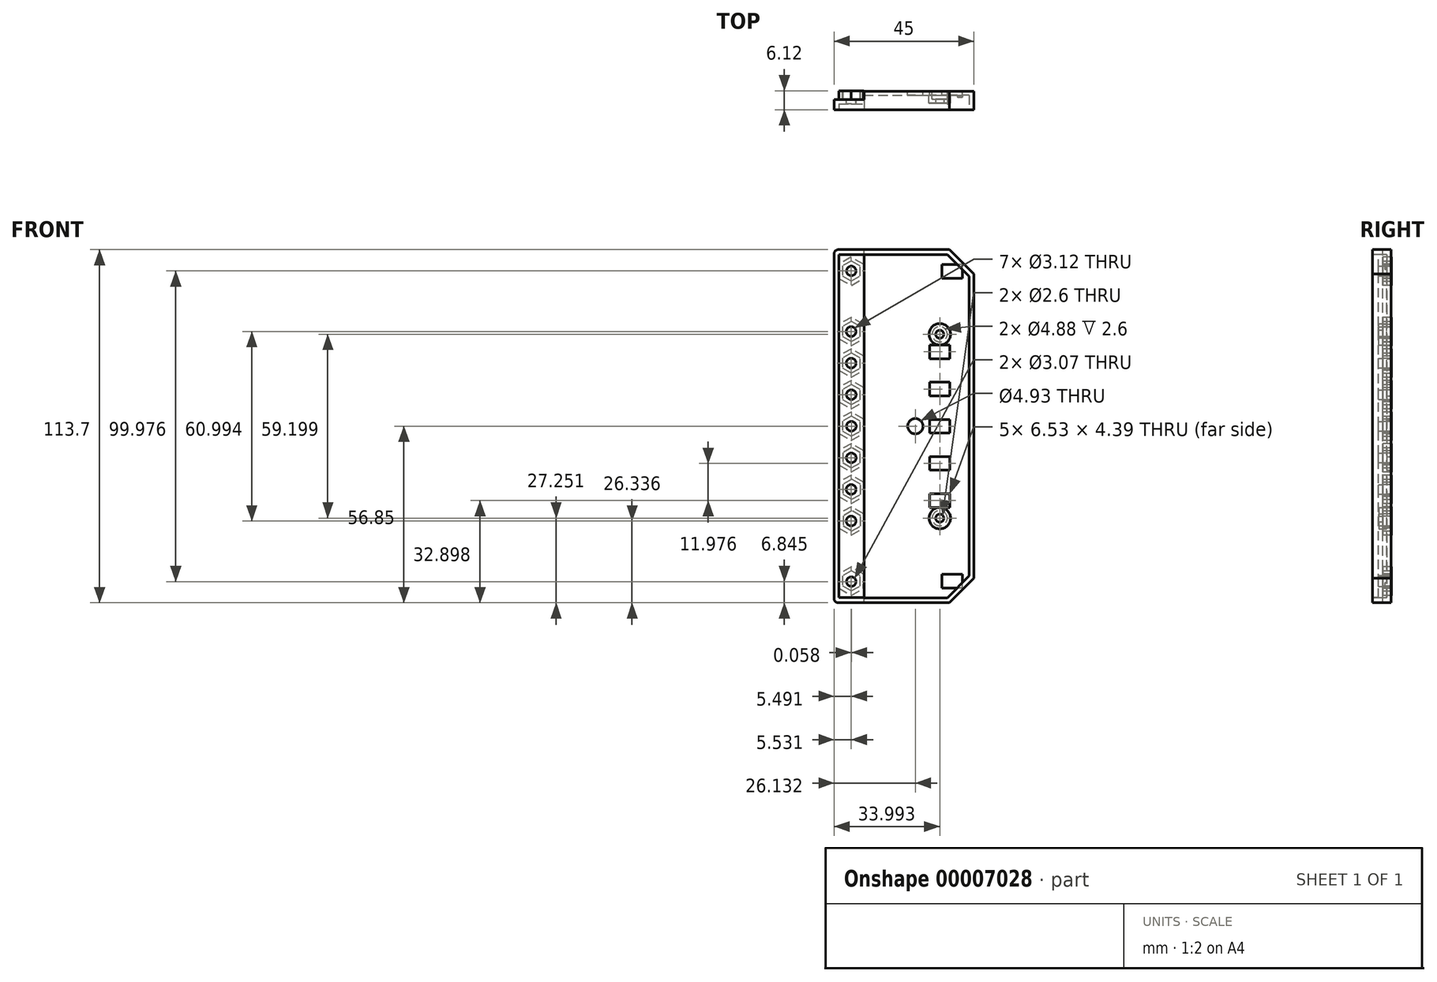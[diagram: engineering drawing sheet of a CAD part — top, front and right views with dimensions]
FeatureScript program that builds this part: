
annotation { "Feature Type Name" : "Feature", "Feature Type Description" : "" }
export const myFeature = defineFeature(function(context is Context, id is Id, definition is map)
    precondition{}
    {
        {
            var Q0;
            Q0=qCreatedBy(makeId("Top.planeOp"),FACE);
            var sketch = newSketch(context, id + "F0", { "sketchPlane" : qUnion([Q0])});
            skLineSegment(sketch, "E0.rect.bottom", {"start": v(22.5, -3) * mm, "end": v(-22.5, -3) * mm});
            skLineSegment(sketch, "E0.rect.top", {"start": v(22.5, 3) * mm, "end": v(-22.5, 3) * mm});
            skLineSegment(sketch, "E0.rect.left", {"start": v(22.5, -3) * mm, "end": v(22.5, 3) * mm});
            skLineSegment(sketch, "E0.rect.right", {"start": v(-22.5, -3) * mm, "end": v(-22.5, 3) * mm});
            skPoint(sketch, "E0.rect.middle", {"position": v(0, 0) * mm});
            skLineSegment(sketch, "E1", {"start": v(-12.85, 3) * mm, "end": v(-12.85, 0.3) * mm});
            skLineSegment(sketch, "E2", {"start": v(-12.85, 0.3) * mm, "end": v(-22.5, 0.3) * mm});
            skSolve(sketch);
        }
        {
            var Q0;
            Q0 = qSketchRegion(id + "F0", true);
            extrude(context, id + "F1", {"entities" : qUnion([Q0]), "oppositeDirection" : true, "depth" : 113.7 * mm});
        }
        {
            var Q0;
            {var subQ1=sQuery(id+"F0.wireOp",EDGE,"E1");Q0=makeQuery(id+"F0.imprint","IMPRINT",FACE,{"disambiguationData":[TD([[makeQuery(id+"F0.imprint","IMPRINT",EDGE,{"derivedFrom":subQ1}),-1.0]])]});}
            extrude(context, id + "F2", {"entities" : qUnion([Q0]), "operationType" : NewBodyOperationType.REMOVE, "oppositeDirection" : true, "depth" : 113.93 * mm});
        }
        {
            var Q0;
            Q0=makeQuery(id+"F1.opExtrude","SWEPT_FACE",FACE,{"disambiguationData":[OSD([sQuery(id+"F0.wireOp",EDGE,"E0.rect.bottom")])]});
            var sketch = newSketch(context, id + "F3", { "sketchPlane" : qUnion([Q0])});
            skLineSegment(sketch, "E3.bottom", {"start": v(-22.5, -113.59) * mm, "end": v(-12.85, -113.59) * mm});
            skLineSegment(sketch, "E3.top", {"start": v(-22.5, 0) * mm, "end": v(-12.85, 0) * mm});
            skLineSegment(sketch, "E3.left", {"start": v(-22.5, -113.59) * mm, "end": v(-22.5, 0) * mm});
            skLineSegment(sketch, "E3.right", {"start": v(-12.85, -113.59) * mm, "end": v(-12.85, 0) * mm});
            skLineSegment(sketch, "E4.bottom", {"start": v(-20.92, -112) * mm, "end": v(-12.85, -112) * mm});
            skLineSegment(sketch, "E4.top", {"start": v(-20.92, -1.58) * mm, "end": v(-12.85, -1.58) * mm});
            skLineSegment(sketch, "E4.left", {"start": v(-20.92, -112) * mm, "end": v(-20.92, -1.58) * mm});
            skLineSegment(sketch, "E4.right", {"start": v(-12.85, -112) * mm, "end": v(-12.85, -1.58) * mm});
            skSolve(sketch);
        }
        {
            var Q0;
            Q0=makeQuery(id+"F3.imprint","IMPRINT",FACE,{"disambiguationData":[TD([[makeQuery(id+"F3.imprint","IMPRINT",EDGE,{"derivedFrom":sQuery(id+"F3.wireOp",EDGE,"E4.bottom")}),1.0]])]});
            extrude(context, id + "F4", {"entities" : qUnion([Q0]), "operationType" : NewBodyOperationType.REMOVE, "oppositeDirection" : true, "depth" : 1.9 * mm});
        }
        {
            var Q0;
            Q0=makeQuery(id+"F1.opExtrude","CAP_EDGE",EDGE,{"disambiguationData":[OSD([sQuery(id+"F0.wireOp",EDGE,"E0.rect.left")])],"isStart":false});
            chamfer(context, id + "F5", {"entities" : qUnion([Q0]), "width" : 7.87 * mm, "tangentPropagation" : true});
        }
        {
            var Q0;
            Q0=makeQuery(id+"F1.opExtrude","CAP_EDGE",EDGE,{"disambiguationData":[OSD([sQuery(id+"F0.wireOp",EDGE,"E0.rect.left")])],"isStart":true});
            chamfer(context, id + "F6", {"entities" : qUnion([Q0]), "width" : 7.87 * mm, "tangentPropagation" : true});
        }
        {
            var Q0;
            Q0=makeQuery(id+"F1.opExtrude","SWEPT_FACE",FACE,{"disambiguationData":[OSD([sQuery(id+"F0.wireOp",EDGE,"E0.rect.bottom")])]});
            var sketch = newSketch(context, id + "F7", { "sketchPlane" : qUnion([Q0])});
            skLineSegment(sketch, "E5.bottom", {"start": v(-12.85, -1.58) * mm, "end": v(21, -1.58) * mm});
            skLineSegment(sketch, "E5.top", {"start": v(-12.85, -112.15) * mm, "end": v(21, -112.15) * mm});
            skLineSegment(sketch, "E5.left", {"start": v(-12.85, -1.58) * mm, "end": v(-12.85, -112.15) * mm});
            skLineSegment(sketch, "E5.right", {"start": v(21, -1.58) * mm, "end": v(21, -112.15) * mm});
            skLineSegment(sketch, "E6", {"start": v(21, -105.06) * mm, "end": v(13.92, -112.15) * mm});
            skLineSegment(sketch, "E7", {"start": v(14, -1.58) * mm, "end": v(21, -8.58) * mm});
            skSolve(sketch);
        }
        {
            var Q0;
            {var subQ3=sQuery(id+"F7.wireOp",EDGE,"E5.left");Q0=makeQuery(id+"F7.imprint","IMPRINT",FACE,{"disambiguationData":[TD([[makeQuery(id+"F7.imprint","IMPRINT",EDGE,{"derivedFrom":subQ3}),-1.0]])]});}
            extrude(context, id + "F8", {"entities" : qUnion([Q0]), "operationType" : NewBodyOperationType.REMOVE, "oppositeDirection" : true, "depth" : 4.67 * mm});
        }
        {
            var Q0;
            Q0=makeQuery(id+"F1.opExtrude","SWEPT_FACE",FACE,{"disambiguationData":[OSD([sQuery(id+"F0.wireOp",EDGE,"E0.rect.top")])]});
            var sketch = newSketch(context, id + "F9", { "sketchPlane" : qUnion([Q0])});
            skLineSegment(sketch, "E8", {"start": v(12.85, -56.85) * mm, "end": v(-22.5, -56.85) * mm, "construction": true});
            skLineSegment(sketch, "E9.rect.bottom", {"start": v(-14.76, -59.05) * mm, "end": v(-8.23, -59.05) * mm});
            skLineSegment(sketch, "E9.rect.top", {"start": v(-14.76, -54.65) * mm, "end": v(-8.23, -54.65) * mm});
            skLineSegment(sketch, "E9.rect.left", {"start": v(-14.76, -59.05) * mm, "end": v(-14.76, -54.65) * mm});
            skLineSegment(sketch, "E9.rect.right", {"start": v(-8.23, -59.05) * mm, "end": v(-8.23, -54.65) * mm});
            skPoint(sketch, "E9.rect.middle", {"position": v(-11.5, -56.85) * mm});
            skCircle(sketch, "E10", {"center": v(-3.63, -56.85) * mm, "radius": 2.46 * mm});
            skLineSegment(sketch, "E11.0.1.0", {"start": v(-8.23, -47.07) * mm, "end": v(-8.23, -42.68) * mm});
            skLineSegment(sketch, "E11.0.1.1", {"start": v(-14.76, -47.07) * mm, "end": v(-8.23, -47.07) * mm});
            skLineSegment(sketch, "E11.0.1.2", {"start": v(-14.76, -47.07) * mm, "end": v(-14.76, -42.68) * mm});
            skLineSegment(sketch, "E11.0.1.3", {"start": v(-14.76, -42.68) * mm, "end": v(-8.23, -42.68) * mm});
            skLineSegment(sketch, "E11.0.2.0", {"start": v(-8.23, -35.1) * mm, "end": v(-8.23, -30.7) * mm});
            skLineSegment(sketch, "E11.0.2.1", {"start": v(-14.76, -35.1) * mm, "end": v(-8.23, -35.1) * mm});
            skLineSegment(sketch, "E11.0.2.2", {"start": v(-14.76, -35.1) * mm, "end": v(-14.76, -30.7) * mm});
            skLineSegment(sketch, "E11.0.2.3", {"start": v(-14.76, -30.7) * mm, "end": v(-8.23, -30.7) * mm});
            skLineSegment(sketch, "E11.direction1", {"start": v(-8.23, -59.05) * mm, "end": v(17.17, -59.05) * mm, "construction": true});
            skLineSegment(sketch, "E11.direction2", {"start": v(-8.23, -59.05) * mm, "end": v(-8.23, -47.07) * mm, "construction": true});
            skLineSegment(sketch, "E12.0.1.0", {"start": v(-8.23, -71.02) * mm, "end": v(-8.23, -66.63) * mm});
            skLineSegment(sketch, "E12.0.1.1", {"start": v(-14.76, -71.02) * mm, "end": v(-8.23, -71.02) * mm});
            skLineSegment(sketch, "E12.0.1.2", {"start": v(-14.76, -71.02) * mm, "end": v(-14.76, -66.63) * mm});
            skLineSegment(sketch, "E12.0.1.3", {"start": v(-14.76, -66.63) * mm, "end": v(-8.23, -66.63) * mm});
            skLineSegment(sketch, "E12.0.2.0", {"start": v(-8.23, -83) * mm, "end": v(-8.23, -78.6) * mm});
            skLineSegment(sketch, "E12.0.2.1", {"start": v(-14.76, -83) * mm, "end": v(-8.23, -83) * mm});
            skLineSegment(sketch, "E12.0.2.2", {"start": v(-14.76, -83) * mm, "end": v(-14.76, -78.6) * mm});
            skLineSegment(sketch, "E12.0.2.3", {"start": v(-14.76, -78.6) * mm, "end": v(-8.23, -78.6) * mm});
            skLineSegment(sketch, "E12.direction2", {"start": v(-8.23, -59.05) * mm, "end": v(-8.23, -71.02) * mm, "construction": true});
            skLineSegment(sketch, "E13.rect.bottom", {"start": v(-18.73, -9.2) * mm, "end": v(-12.2, -9.2) * mm});
            skLineSegment(sketch, "E13.rect.top", {"start": v(-18.73, -4.8) * mm, "end": v(-12.2, -4.8) * mm});
            skLineSegment(sketch, "E13.rect.left", {"start": v(-18.73, -9.2) * mm, "end": v(-18.73, -4.8) * mm});
            skLineSegment(sketch, "E13.rect.right", {"start": v(-12.2, -9.2) * mm, "end": v(-12.2, -4.8) * mm});
            skPoint(sketch, "E13.rect.middle", {"position": v(-15.47, -7) * mm});
            skLineSegment(sketch, "E14.rect.bottom", {"start": v(-18.73, -108.9) * mm, "end": v(-12.2, -108.9) * mm});
            skLineSegment(sketch, "E14.rect.top", {"start": v(-18.73, -104.5) * mm, "end": v(-12.2, -104.5) * mm});
            skLineSegment(sketch, "E14.rect.left", {"start": v(-18.73, -108.9) * mm, "end": v(-18.73, -104.5) * mm});
            skLineSegment(sketch, "E14.rect.right", {"start": v(-12.2, -108.9) * mm, "end": v(-12.2, -104.5) * mm});
            skPoint(sketch, "E14.rect.middle", {"position": v(-15.47, -106.7) * mm});
            skSolve(sketch);
        }
        {
            var Q0;
            Q0 = qSketchRegion(id + "F9", true);
            extrude(context, id + "F10", {"entities" : qUnion([Q0]), "operationType" : NewBodyOperationType.REMOVE, "oppositeDirection" : true, "depth" : 2 * mm});
        }
        {
            var Q0;
            Q0=makeQuery(id+"F8.boolean.opBoolean","COPY",FACE,{"derivedFrom":makeQuery(id+"F8.opExtrude","CAP_FACE",FACE,{"disambiguationData":[OSD([sQuery(id+"F7.wireOp",EDGE,"E5.bottom"),sQuery(id+"F7.wireOp",EDGE,"E5.top"),sQuery(id+"F7.wireOp",EDGE,"E5.left"),sQuery(id+"F7.wireOp",EDGE,"E5.right"),sQuery(id+"F7.wireOp",EDGE,"E6"),sQuery(id+"F7.wireOp",EDGE,"E7")])],"isStart":false})});
            var sketch = newSketch(context, id + "F11", { "sketchPlane" : qUnion([Q0])});
            skCircle(sketch, "E15", {"center": v(11.5, -27.25) * mm, "radius": 3.45 * mm});
            skCircle(sketch, "E16", {"center": v(11.5, -86.45) * mm, "radius": 3.45 * mm});
            skPoint(sketch, "E17", {"position": v(11.5, -30.7) * mm});
            skPoint(sketch, "E18", {"position": v(11.5, -83) * mm});
            skSolve(sketch);
        }
        {
            var Q0;
            Q0 = qSketchRegion(id + "F11", true);
            extrude(context, id + "F12", {"entities" : qUnion([Q0]), "operationType" : NewBodyOperationType.ADD, "depth" : 2.6 * mm});
        }
        {
            var Q0;
            Q0=makeQuery(id+"F12.opExtrude","CAP_FACE",FACE,{"disambiguationData":[OSD([sQuery(id+"F11.wireOp",EDGE,"E16")])],"isStart":false});
            var sketch = newSketch(context, id + "F13", { "sketchPlane" : qUnion([Q0])});
            skCircle(sketch, "E19", {"center": v(11.5, -86.45) * mm, "radius": 1.3 * mm});
            skCircle(sketch, "E20", {"center": v(11.5, -27.25) * mm, "radius": 1.3 * mm});
            skSolve(sketch);
        }
        {
            var Q0;
            Q0 = qSketchRegion(id + "F13", true);
            extrude(context, id + "F14", {"entities" : qUnion([Q0]), "operationType" : NewBodyOperationType.REMOVE, "oppositeDirection" : true, "depth" : 25 * mm});
        }
        {
            var Q0;
            Q0=makeQuery(id+"F1.opExtrude","SWEPT_FACE",FACE,{"disambiguationData":[OSD([sQuery(id+"F0.wireOp",EDGE,"E0.rect.top")])]});
            var sketch = newSketch(context, id + "F15", { "sketchPlane" : qUnion([Q0])});
            skCircle(sketch, "E21", {"center": v(-11.5, -27.25) * mm, "radius": 2.44 * mm});
            skCircle(sketch, "E22", {"center": v(-11.5, -86.45) * mm, "radius": 2.44 * mm});
            skSolve(sketch);
        }
        {
            var Q0;
            Q0 = qSketchRegion(id + "F15", true);
            extrude(context, id + "F16", {"entities" : qUnion([Q0]), "operationType" : NewBodyOperationType.REMOVE, "oppositeDirection" : true, "depth" : 2.6 * mm});
        }
        {
            var Q0;
            Q0=makeQuery(id+"F1.opExtrude","CAP_EDGE",EDGE,{"disambiguationData":[OSD([sQuery(id+"F0.wireOp",EDGE,"E0.rect.right")])],"isStart":true});
            var Q1;
            Q1=makeQuery(id+"F1.opExtrude","CAP_EDGE",EDGE,{"disambiguationData":[OSD([sQuery(id+"F0.wireOp",EDGE,"E0.rect.right")])],"isStart":false});
            fillet(context, id + "F17", {"entities" : qUnion([Q0, Q1]), "radius" : 1.4 * mm, "tangentPropagation" : true, "allowEdgeOverflow" : false});
        }
        {
            var Q0;
            Q0=makeQuery(id+"F2.boolean.opBoolean","COPY",FACE,{"derivedFrom":makeQuery(id+"F2.opExtrude","SWEPT_FACE",FACE,{"disambiguationData":[OSD([sQuery(id+"F0.wireOp",EDGE,"E2")])]})});
            var sketch = newSketch(context, id + "F18", { "sketchPlane" : qUnion([Q0])});
            skCircle(sketch, "E23.cCircle", {"center": v(16.97, -56.85) * mm, "radius": 3.96 * mm, "construction": true});
            skLineSegment(sketch, "E23.0", {"start": v(16.95, -52.27) * mm, "end": v(20.92, -54.54) * mm});
            skLineSegment(sketch, "E23.1", {"start": v(20.92, -54.54) * mm, "end": v(20.95, -59.12) * mm});
            skLineSegment(sketch, "E23.2", {"start": v(20.95, -59.12) * mm, "end": v(17, -61.43) * mm});
            skLineSegment(sketch, "E23.3", {"start": v(17, -61.43) * mm, "end": v(13.02, -59.16) * mm});
            skLineSegment(sketch, "E23.4", {"start": v(13.02, -59.16) * mm, "end": v(13, -54.58) * mm});
            skLineSegment(sketch, "E23.5", {"start": v(13, -54.58) * mm, "end": v(16.95, -52.27) * mm});
            skPoint(sketch, "E23.0.midPoint", {"position": v(18.94, -53.4) * mm});
            skLineSegment(sketch, "E24", {"start": v(16.97, 0) * mm, "end": v(16.97, -113.7) * mm});
            skLineSegment(sketch, "E25.0.1.0", {"start": v(13, -44.42) * mm, "end": v(16.95, -42.11) * mm});
            skLineSegment(sketch, "E25.0.1.1", {"start": v(13.02, -49) * mm, "end": v(13, -44.42) * mm});
            skLineSegment(sketch, "E25.0.1.2", {"start": v(17, -51.27) * mm, "end": v(13.02, -49) * mm});
            skLineSegment(sketch, "E25.0.1.3", {"start": v(20.95, -48.96) * mm, "end": v(17, -51.27) * mm});
            skLineSegment(sketch, "E25.0.1.4", {"start": v(20.92, -44.38) * mm, "end": v(20.95, -48.96) * mm});
            skLineSegment(sketch, "E25.0.1.5", {"start": v(16.95, -42.11) * mm, "end": v(20.92, -44.38) * mm});
            skLineSegment(sketch, "E25.0.2.0", {"start": v(13, -34.26) * mm, "end": v(16.95, -31.95) * mm});
            skLineSegment(sketch, "E25.0.2.1", {"start": v(13.02, -38.84) * mm, "end": v(13, -34.26) * mm});
            skLineSegment(sketch, "E25.0.2.2", {"start": v(17, -41.1) * mm, "end": v(13.02, -38.84) * mm});
            skLineSegment(sketch, "E25.0.2.3", {"start": v(20.95, -38.8) * mm, "end": v(17, -41.1) * mm});
            skLineSegment(sketch, "E25.0.2.4", {"start": v(20.92, -34.22) * mm, "end": v(20.95, -38.8) * mm});
            skLineSegment(sketch, "E25.0.2.5", {"start": v(16.95, -31.95) * mm, "end": v(20.92, -34.22) * mm});
            skLineSegment(sketch, "E25.0.3.0", {"start": v(13, -24.1) * mm, "end": v(16.95, -21.8) * mm});
            skLineSegment(sketch, "E25.0.3.1", {"start": v(13.02, -28.68) * mm, "end": v(13, -24.1) * mm});
            skLineSegment(sketch, "E25.0.3.2", {"start": v(17, -30.95) * mm, "end": v(13.02, -28.68) * mm});
            skLineSegment(sketch, "E25.0.3.3", {"start": v(20.95, -28.64) * mm, "end": v(17, -30.95) * mm});
            skLineSegment(sketch, "E25.0.3.4", {"start": v(20.92, -24.06) * mm, "end": v(20.95, -28.64) * mm});
            skLineSegment(sketch, "E25.0.3.5", {"start": v(16.95, -21.8) * mm, "end": v(20.92, -24.06) * mm});
            skLineSegment(sketch, "E25.direction1", {"start": v(13, -54.58) * mm, "end": v(38.4, -54.58) * mm, "construction": true});
            skLineSegment(sketch, "E25.direction2", {"start": v(13, -54.58) * mm, "end": v(13, -44.42) * mm, "construction": true});
            skLineSegment(sketch, "E26.1.0.0", {"start": v(13.02, -69.32) * mm, "end": v(13, -64.74) * mm});
            skLineSegment(sketch, "E26.1.0.1", {"start": v(17, -71.59) * mm, "end": v(13.02, -69.32) * mm});
            skLineSegment(sketch, "E26.1.0.2", {"start": v(20.94, -69.28) * mm, "end": v(17, -71.59) * mm});
            skLineSegment(sketch, "E26.1.0.3", {"start": v(20.92, -64.7) * mm, "end": v(20.94, -69.28) * mm});
            skLineSegment(sketch, "E26.1.0.4", {"start": v(16.95, -62.43) * mm, "end": v(20.92, -64.7) * mm});
            skLineSegment(sketch, "E26.1.0.5", {"start": v(13, -64.74) * mm, "end": v(16.95, -62.43) * mm});
            skLineSegment(sketch, "E26.2.0.0", {"start": v(13.01, -79.48) * mm, "end": v(12.99, -74.9) * mm});
            skLineSegment(sketch, "E26.2.0.1", {"start": v(16.99, -81.75) * mm, "end": v(13.01, -79.48) * mm});
            skLineSegment(sketch, "E26.2.0.2", {"start": v(20.94, -79.44) * mm, "end": v(16.99, -81.75) * mm});
            skLineSegment(sketch, "E26.2.0.3", {"start": v(20.91, -74.86) * mm, "end": v(20.94, -79.44) * mm});
            skLineSegment(sketch, "E26.2.0.4", {"start": v(16.94, -72.6) * mm, "end": v(20.91, -74.86) * mm});
            skLineSegment(sketch, "E26.2.0.5", {"start": v(12.99, -74.9) * mm, "end": v(16.94, -72.6) * mm});
            skLineSegment(sketch, "E26.3.0.0", {"start": v(13, -89.64) * mm, "end": v(12.99, -85.06) * mm});
            skLineSegment(sketch, "E26.3.0.1", {"start": v(16.98, -91.9) * mm, "end": v(13, -89.64) * mm});
            skLineSegment(sketch, "E26.3.0.2", {"start": v(20.93, -89.6) * mm, "end": v(16.98, -91.9) * mm});
            skLineSegment(sketch, "E26.3.0.3", {"start": v(20.9, -85.02) * mm, "end": v(20.93, -89.6) * mm});
            skLineSegment(sketch, "E26.3.0.4", {"start": v(16.94, -82.75) * mm, "end": v(20.9, -85.02) * mm});
            skLineSegment(sketch, "E26.3.0.5", {"start": v(12.99, -85.06) * mm, "end": v(16.94, -82.75) * mm});
            skLineSegment(sketch, "E26.direction1", {"start": v(13.02, -59.16) * mm, "end": v(13.02, -69.32) * mm, "construction": true});
            skCircle(sketch, "E27.cCircle", {"center": v(16.97, -7.02) * mm, "radius": 3.96 * mm, "construction": true});
            skLineSegment(sketch, "E27.0", {"start": v(16.93, -11.6) * mm, "end": v(13, -9.27) * mm});
            skLineSegment(sketch, "E27.1", {"start": v(13, -9.27) * mm, "end": v(13.03, -4.7) * mm});
            skLineSegment(sketch, "E27.2", {"start": v(13.03, -4.7) * mm, "end": v(17.02, -2.44) * mm});
            skLineSegment(sketch, "E27.3", {"start": v(17.02, -2.44) * mm, "end": v(20.96, -4.77) * mm});
            skLineSegment(sketch, "E27.4", {"start": v(20.96, -4.77) * mm, "end": v(20.91, -9.34) * mm});
            skLineSegment(sketch, "E27.5", {"start": v(20.91, -9.34) * mm, "end": v(16.93, -11.6) * mm});
            skPoint(sketch, "E27.0.midPoint", {"position": v(14.96, -10.43) * mm});
            skCircle(sketch, "E28.cCircle", {"center": v(16.97, -106.72) * mm, "radius": 3.96 * mm, "construction": true});
            skLineSegment(sketch, "E28.0", {"start": v(13, -104.47) * mm, "end": v(16.93, -102.15) * mm});
            skLineSegment(sketch, "E28.1", {"start": v(16.93, -102.15) * mm, "end": v(20.91, -104.4) * mm});
            skLineSegment(sketch, "E28.2", {"start": v(20.91, -104.4) * mm, "end": v(20.96, -108.97) * mm});
            skLineSegment(sketch, "E28.3", {"start": v(20.96, -108.97) * mm, "end": v(17.02, -111.3) * mm});
            skLineSegment(sketch, "E28.4", {"start": v(17.02, -111.3) * mm, "end": v(13.03, -109.05) * mm});
            skLineSegment(sketch, "E28.5", {"start": v(13.03, -109.05) * mm, "end": v(13, -104.47) * mm});
            skPoint(sketch, "E28.0.midPoint", {"position": v(14.96, -103.3) * mm});
            skSolve(sketch);
        }
        {
            var Q0;
            Q0 = qSketchRegion(id + "F18", true);
            extrude(context, id + "F19", {"entities" : qUnion([Q0]), "operationType" : NewBodyOperationType.ADD, "depth" : 2.82 * mm});
        }
        {
            var Q0;
            Q0=makeQuery(id+"F19.opExtrude","CAP_FACE",FACE,{"disambiguationData":[OSD([sQuery(id+"F18.wireOp",EDGE,"E23.0"),sQuery(id+"F18.wireOp",EDGE,"E23.1"),sQuery(id+"F18.wireOp",EDGE,"E23.2"),sQuery(id+"F18.wireOp",EDGE,"E23.3"),sQuery(id+"F18.wireOp",EDGE,"E23.4"),sQuery(id+"F18.wireOp",EDGE,"E23.5")])],"isStart":false});
            var sketch = newSketch(context, id + "F20", { "sketchPlane" : qUnion([Q0])});
            skCircle(sketch, "E29.cCircle", {"center": v(16.95, -56.85) * mm, "radius": 2.82 * mm, "construction": true});
            skLineSegment(sketch, "E29.0", {"start": v(16.93, -53.6) * mm, "end": v(19.76, -55.2) * mm});
            skLineSegment(sketch, "E29.1", {"start": v(19.76, -55.2) * mm, "end": v(19.78, -58.46) * mm});
            skLineSegment(sketch, "E29.2", {"start": v(19.78, -58.46) * mm, "end": v(16.97, -60.1) * mm});
            skLineSegment(sketch, "E29.3", {"start": v(16.97, -60.1) * mm, "end": v(14.14, -58.5) * mm});
            skLineSegment(sketch, "E29.4", {"start": v(14.14, -58.5) * mm, "end": v(14.12, -55.24) * mm});
            skLineSegment(sketch, "E29.5", {"start": v(14.12, -55.24) * mm, "end": v(16.93, -53.6) * mm});
            skPoint(sketch, "E29.0.midPoint", {"position": v(18.35, -54.4) * mm});
            skLineSegment(sketch, "E30", {"start": v(16.95, 0) * mm, "end": v(16.95, -113.7) * mm, "construction": true});
            skLineSegment(sketch, "E31.0.1.0", {"start": v(19.76, -45.05) * mm, "end": v(19.78, -48.3) * mm});
            skLineSegment(sketch, "E31.0.1.1", {"start": v(16.93, -43.43) * mm, "end": v(19.76, -45.05) * mm});
            skLineSegment(sketch, "E31.0.1.2", {"start": v(14.12, -45.08) * mm, "end": v(16.93, -43.43) * mm});
            skLineSegment(sketch, "E31.0.1.3", {"start": v(14.14, -48.33) * mm, "end": v(14.12, -45.08) * mm});
            skLineSegment(sketch, "E31.0.1.4", {"start": v(16.97, -49.95) * mm, "end": v(14.14, -48.33) * mm});
            skLineSegment(sketch, "E31.0.1.5", {"start": v(19.78, -48.3) * mm, "end": v(16.97, -49.95) * mm});
            skLineSegment(sketch, "E31.0.2.0", {"start": v(19.76, -34.89) * mm, "end": v(19.78, -38.14) * mm});
            skLineSegment(sketch, "E31.0.2.1", {"start": v(16.93, -33.27) * mm, "end": v(19.76, -34.89) * mm});
            skLineSegment(sketch, "E31.0.2.2", {"start": v(14.12, -34.92) * mm, "end": v(16.93, -33.27) * mm});
            skLineSegment(sketch, "E31.0.2.3", {"start": v(14.14, -38.17) * mm, "end": v(14.12, -34.92) * mm});
            skLineSegment(sketch, "E31.0.2.4", {"start": v(16.97, -39.79) * mm, "end": v(14.14, -38.17) * mm});
            skLineSegment(sketch, "E31.0.2.5", {"start": v(19.78, -38.14) * mm, "end": v(16.97, -39.79) * mm});
            skLineSegment(sketch, "E31.0.3.0", {"start": v(19.76, -24.73) * mm, "end": v(19.78, -27.98) * mm});
            skLineSegment(sketch, "E31.0.3.1", {"start": v(16.93, -23.11) * mm, "end": v(19.76, -24.73) * mm});
            skLineSegment(sketch, "E31.0.3.2", {"start": v(14.12, -24.76) * mm, "end": v(16.93, -23.11) * mm});
            skLineSegment(sketch, "E31.0.3.3", {"start": v(14.14, -28.01) * mm, "end": v(14.12, -24.76) * mm});
            skLineSegment(sketch, "E31.0.3.4", {"start": v(16.97, -29.63) * mm, "end": v(14.14, -28.01) * mm});
            skLineSegment(sketch, "E31.0.3.5", {"start": v(19.78, -27.98) * mm, "end": v(16.97, -29.63) * mm});
            skLineSegment(sketch, "E31.direction1", {"start": v(19.78, -58.46) * mm, "end": v(45.18, -58.46) * mm, "construction": true});
            skLineSegment(sketch, "E31.direction2", {"start": v(19.78, -58.46) * mm, "end": v(19.78, -48.3) * mm, "construction": true});
            skLineSegment(sketch, "E32.1.0.0", {"start": v(14.08, -68.65) * mm, "end": v(14.06, -65.4) * mm});
            skLineSegment(sketch, "E32.1.0.1", {"start": v(14.06, -65.4) * mm, "end": v(16.87, -63.75) * mm});
            skPoint(sketch, "E32.1.0.2", {"position": v(18.29, -64.56) * mm});
            skLineSegment(sketch, "E32.1.0.3", {"start": v(19.7, -65.37) * mm, "end": v(19.72, -68.62) * mm});
            skLineSegment(sketch, "E32.1.0.4", {"start": v(16.87, -63.75) * mm, "end": v(19.7, -65.37) * mm});
            skLineSegment(sketch, "E32.1.0.5", {"start": v(19.72, -68.62) * mm, "end": v(16.91, -70.27) * mm});
            skLineSegment(sketch, "E32.1.0.6", {"start": v(16.91, -70.27) * mm, "end": v(14.08, -68.65) * mm});
            skLineSegment(sketch, "E32.2.0.0", {"start": v(14.03, -78.81) * mm, "end": v(14, -75.56) * mm});
            skLineSegment(sketch, "E32.2.0.1", {"start": v(14, -75.56) * mm, "end": v(16.82, -73.91) * mm});
            skPoint(sketch, "E32.2.0.2", {"position": v(18.23, -74.72) * mm});
            skLineSegment(sketch, "E32.2.0.3", {"start": v(19.65, -75.53) * mm, "end": v(19.67, -78.78) * mm});
            skLineSegment(sketch, "E32.2.0.4", {"start": v(16.82, -73.91) * mm, "end": v(19.65, -75.53) * mm});
            skLineSegment(sketch, "E32.2.0.5", {"start": v(19.67, -78.78) * mm, "end": v(16.86, -80.43) * mm});
            skLineSegment(sketch, "E32.2.0.6", {"start": v(16.86, -80.43) * mm, "end": v(14.03, -78.81) * mm});
            skLineSegment(sketch, "E32.3.0.0", {"start": v(13.97, -88.97) * mm, "end": v(13.95, -85.72) * mm});
            skLineSegment(sketch, "E32.3.0.1", {"start": v(13.95, -85.72) * mm, "end": v(16.76, -84.07) * mm});
            skPoint(sketch, "E32.3.0.2", {"position": v(18.17, -84.88) * mm});
            skLineSegment(sketch, "E32.3.0.3", {"start": v(19.59, -85.68) * mm, "end": v(19.6, -88.94) * mm});
            skLineSegment(sketch, "E32.3.0.4", {"start": v(16.76, -84.07) * mm, "end": v(19.59, -85.68) * mm});
            skLineSegment(sketch, "E32.3.0.5", {"start": v(19.6, -88.94) * mm, "end": v(16.8, -90.59) * mm});
            skLineSegment(sketch, "E32.3.0.6", {"start": v(16.8, -90.59) * mm, "end": v(13.97, -88.97) * mm});
            skLineSegment(sketch, "E32.direction1", {"start": v(14.14, -58.5) * mm, "end": v(14.08, -68.65) * mm, "construction": true});
            skCircle(sketch, "E33.cCircle", {"center": v(16.95, -106.62) * mm, "radius": 2.82 * mm, "construction": true});
            skLineSegment(sketch, "E33.0", {"start": v(14.12, -105) * mm, "end": v(16.94, -103.36) * mm});
            skLineSegment(sketch, "E33.1", {"start": v(16.94, -103.36) * mm, "end": v(19.76, -104.98) * mm});
            skLineSegment(sketch, "E33.2", {"start": v(19.76, -104.98) * mm, "end": v(19.78, -108.24) * mm});
            skLineSegment(sketch, "E33.3", {"start": v(19.78, -108.24) * mm, "end": v(16.96, -109.88) * mm});
            skLineSegment(sketch, "E33.4", {"start": v(16.96, -109.88) * mm, "end": v(14.14, -108.26) * mm});
            skLineSegment(sketch, "E33.5", {"start": v(14.14, -108.26) * mm, "end": v(14.12, -105) * mm});
            skPoint(sketch, "E33.0.midPoint", {"position": v(15.53, -104.18) * mm});
            skCircle(sketch, "E34.cCircle", {"center": v(16.95, -6.88) * mm, "radius": 2.82 * mm, "construction": true});
            skPoint(sketch, "E34.cCircle.perimeterSnap0", {"position": v(15.56, -38.98) * mm});
            skLineSegment(sketch, "E34.0", {"start": v(14.12, -5.26) * mm, "end": v(16.93, -3.62) * mm});
            skLineSegment(sketch, "E34.1", {"start": v(16.93, -3.62) * mm, "end": v(19.76, -5.23) * mm});
            skLineSegment(sketch, "E34.2", {"start": v(19.76, -5.23) * mm, "end": v(19.78, -8.49) * mm});
            skLineSegment(sketch, "E34.3", {"start": v(19.78, -8.49) * mm, "end": v(16.97, -10.13) * mm});
            skLineSegment(sketch, "E34.4", {"start": v(16.97, -10.13) * mm, "end": v(14.14, -8.52) * mm});
            skLineSegment(sketch, "E34.5", {"start": v(14.14, -8.52) * mm, "end": v(14.12, -5.26) * mm});
            skPoint(sketch, "E34.0.midPoint", {"position": v(15.53, -4.44) * mm});
            skSolve(sketch);
        }
        {
            var Q0;
            Q0 = qSketchRegion(id + "F20", true);
            extrude(context, id + "F21", {"entities" : qUnion([Q0]), "operationType" : NewBodyOperationType.REMOVE, "oppositeDirection" : true, "depth" : 2.82 * mm});
        }
        {
            var Q0;
            Q0=makeQuery(id+"F21.boolean.opBoolean","COPY",FACE,{"derivedFrom":makeQuery(id+"F21.opExtrude","CAP_FACE",FACE,{"disambiguationData":[OSD([sQuery(id+"F20.wireOp",EDGE,"E29.0"),sQuery(id+"F20.wireOp",EDGE,"E29.1"),sQuery(id+"F20.wireOp",EDGE,"E29.2"),sQuery(id+"F20.wireOp",EDGE,"E29.3"),sQuery(id+"F20.wireOp",EDGE,"E29.4"),sQuery(id+"F20.wireOp",EDGE,"E29.5")])],"isStart":false})});
            var sketch = newSketch(context, id + "F22", { "sketchPlane" : qUnion([Q0])});
            skLineSegment(sketch, "E35", {"start": v(16.93, -53.6) * mm, "end": v(16.97, -60.1) * mm, "construction": true});
            skCircle(sketch, "E36", {"center": v(16.95, -56.85) * mm, "radius": 1.56 * mm});
            skCircle(sketch, "E37.0.1.0", {"center": v(16.97, -46.7) * mm, "radius": 1.56 * mm});
            skCircle(sketch, "E37.0.2.0", {"center": v(16.99, -36.53) * mm, "radius": 1.56 * mm});
            skCircle(sketch, "E37.0.3.0", {"center": v(17, -26.37) * mm, "radius": 1.56 * mm});
            skLineSegment(sketch, "E37.direction1", {"start": v(16.95, -56.85) * mm, "end": v(42.35, -56.85) * mm, "construction": true});
            skLineSegment(sketch, "E37.direction2", {"start": v(16.95, -56.85) * mm, "end": v(16.97, -46.7) * mm, "construction": true});
            skCircle(sketch, "E38", {"center": v(16.97, -6.88) * mm, "radius": 1.54 * mm});
            skLineSegment(sketch, "E39", {"start": v(16.97, -10.13) * mm, "end": v(16.97, -3.63) * mm, "construction": true});
            skLineSegment(sketch, "E40", {"start": v(14.13, -56.87) * mm, "end": v(19.77, -56.87) * mm, "construction": true});
            skCircle(sketch, "E41.MirrorC", {"center": v(16.97, -67.04) * mm, "radius": 1.56 * mm});
            skCircle(sketch, "E42.MirrorC", {"center": v(16.99, -77.2) * mm, "radius": 1.56 * mm});
            skCircle(sketch, "E43.MirrorC", {"center": v(17, -87.36) * mm, "radius": 1.56 * mm});
            skCircle(sketch, "E44.MirrorC", {"center": v(16.97, -106.86) * mm, "radius": 1.54 * mm});
            skSolve(sketch);
        }
        {
            var Q0;
            Q0 = qSketchRegion(id + "F22", true);
            extrude(context, id + "F23", {"entities" : qUnion([Q0]), "operationType" : NewBodyOperationType.REMOVE, "oppositeDirection" : true, "depth" : 25.4 * mm});
        }
    });
